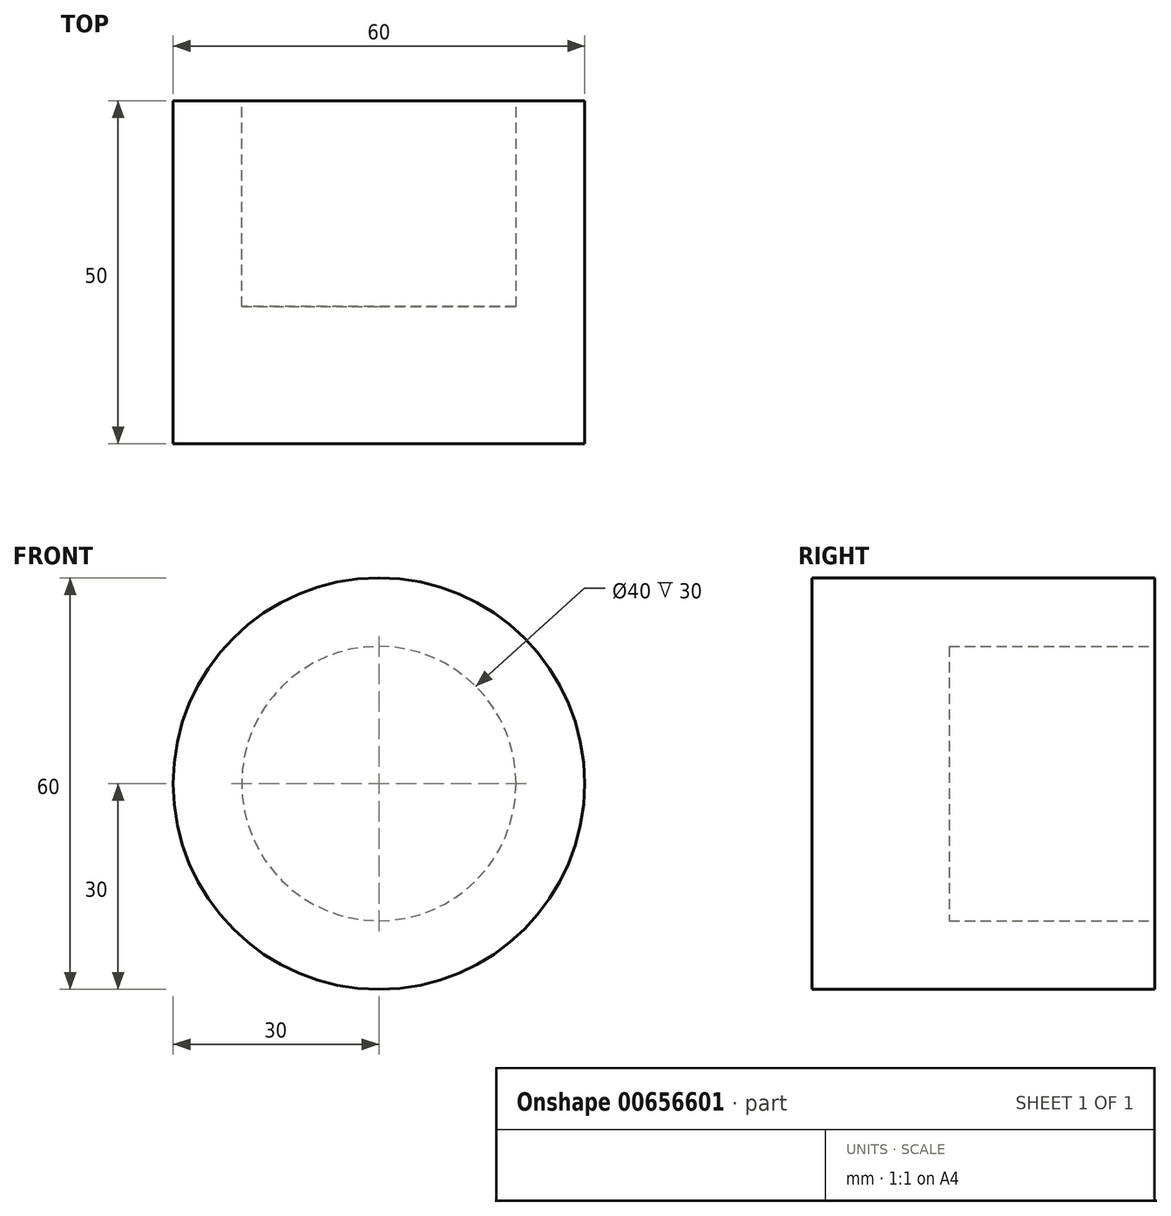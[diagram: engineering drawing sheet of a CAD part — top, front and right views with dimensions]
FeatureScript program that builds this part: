
annotation { "Feature Type Name" : "Feature", "Feature Type Description" : "" }
export const myFeature = defineFeature(function(context is Context, id is Id, definition is map)
    precondition{}
    {
        {
            var Q0;
            Q0=qCreatedBy(makeId("Front.planeOp"),FACE);
            var sketch = newSketch(context, id + "F0", { "sketchPlane" : qUnion([Q0])});
            skCircle(sketch, "E0", {"center": v(0, 0) * mm, "radius": 30 * mm});
            skSolve(sketch);
        }
        {
            var Q0;
            Q0 = qSketchRegion(id + "F0", true);
            extrude(context, id + "F1", {"entities" : qUnion([Q0]), "endBound" : BoundingType.SYMMETRIC, "depth" : 50 * mm, "offsetDistance" : 25.4 * mm});
        }
        {
            var Q0;
            Q0=makeQuery(id+"F1.opExtrude","CAP_FACE",FACE,{"disambiguationData":[OSD([sQuery(id+"F0.wireOp",EDGE,"E0")])],"isStart":true});
            var sketch = newSketch(context, id + "F2", { "sketchPlane" : qUnion([Q0])});
            skCircle(sketch, "E1", {"center": v(0, 0) * mm, "radius": 20 * mm});
            skSolve(sketch);
        }
        {
            var Q0;
            Q0 = qSketchRegion(id + "F2", true);
            extrude(context, id + "F3", {"entities" : qUnion([Q0]), "operationType" : NewBodyOperationType.REMOVE, "oppositeDirection" : true, "depth" : 30 * mm, "offsetDistance" : 25.4 * mm});
        }
    });
